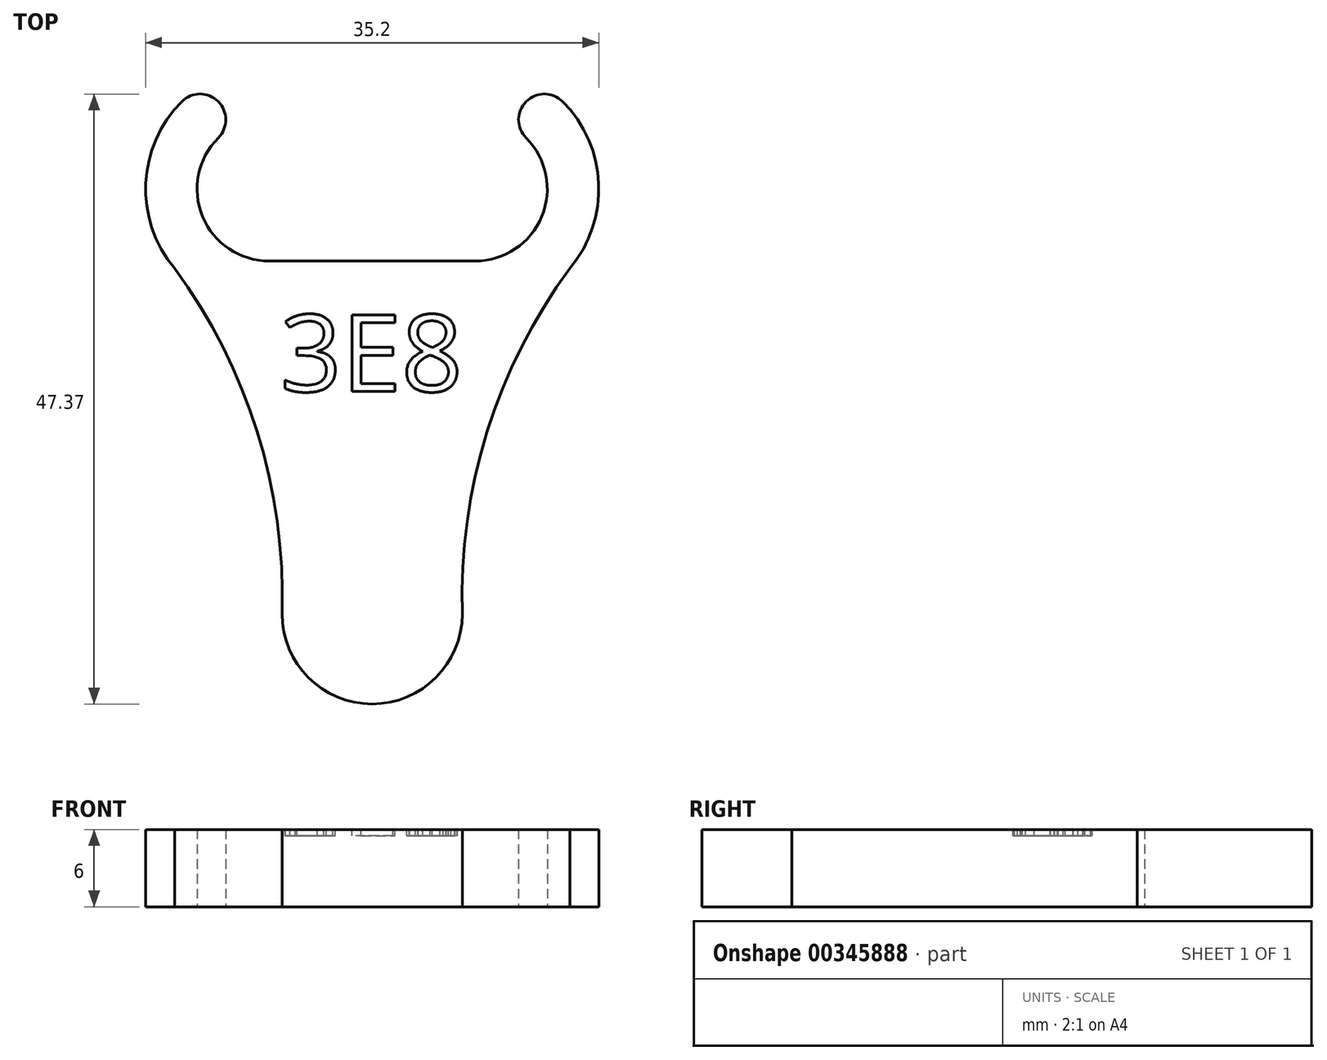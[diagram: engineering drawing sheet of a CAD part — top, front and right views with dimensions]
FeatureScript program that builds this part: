
annotation { "Feature Type Name" : "Feature", "Feature Type Description" : "" }
export const myFeature = defineFeature(function(context is Context, id is Id, definition is map)
    precondition{}
    {
        {
            assignVariable(context, id + "F0", {"name" : "toolthick", "anyValue" : 6});
        }
        {
            var Q0;
            Q0=qCreatedBy(makeId("Top.planeOp"),FACE);
            var sketch = newSketch(context, id + "F1", { "sketchPlane" : qUnion([Q0])});
            skLineSegment(sketch, "E0", {"start": v(-8, 0) * mm, "end": v(8, 0) * mm, "construction": true});
            skCircle(sketch, "E1", {"center": v(-8, 0) * mm, "radius": 5 * mm, "construction": true});
            skCircle(sketch, "E2", {"center": v(8, 0) * mm, "radius": 5 * mm, "construction": true});
            skArc(sketch, "E3", {"start": v(-13.6, 0) * mm, "mid": v(-11.96, -3.96) * mm, "end": v(-8, -5.6) * mm});
            skLineSegment(sketch, "E4", {"start": v(-8, 0) * mm, "end": v(-11.96, 3.96) * mm, "construction": true});
            skArc(sketch, "E5", {"start": v(-11.96, 3.96) * mm, "mid": v(-13.17, 2.14) * mm, "end": v(-13.6, 0) * mm});
            skArc(sketch, "E6", {"start": v(-11.96, 3.96) * mm, "mid": v(-11.96, 6.79) * mm, "end": v(-14.79, 6.79) * mm});
            skLineSegment(sketch, "E7", {"start": v(-11.96, 3.96) * mm, "end": v(-14.79, 6.79) * mm, "construction": true});
            skArc(sketch, "E8", {"start": v(-7, -33) * mm, "mid": v(-4.95, -37.95) * mm, "end": v(0, -40) * mm});
            skLineSegment(sketch, "E9", {"start": v(0, -40) * mm, "end": v(0, 0) * mm, "construction": true});
            skLineSegment(sketch, "E10", {"start": v(-8, -5.6) * mm, "end": v(0, -5.6) * mm});
            skLineSegment(sketch, "E11.MirrorCS", {"start": v(8, -5.6) * mm, "end": v(0, -5.6) * mm});
            skArc(sketch, "E12.MirrorCS", {"start": v(13.6, 0) * mm, "mid": v(11.96, -3.96) * mm, "end": v(8, -5.6) * mm});
            skArc(sketch, "E13.MirrorCS", {"start": v(11.96, 3.96) * mm, "mid": v(13.17, 2.14) * mm, "end": v(13.6, 0) * mm});
            skArc(sketch, "E14.MirrorCS", {"start": v(11.96, 3.96) * mm, "mid": v(11.96, 6.79) * mm, "end": v(14.79, 6.79) * mm});
            skArc(sketch, "E15.MirrorCS", {"start": v(7, -33) * mm, "mid": v(4.95, -37.95) * mm, "end": v(0, -40) * mm});
            skArc(sketch, "E16", {"start": v(-14.79, 6.79) * mm, "mid": v(-17.6, 0.42) * mm, "end": v(-15.35, -6.17) * mm});
            skArc(sketch, "E17.MirrorCS", {"start": v(14.79, 6.79) * mm, "mid": v(17.6, 0.42) * mm, "end": v(15.35, -6.17) * mm});
            skLineSegment(sketch, "E18", {"start": v(0, -33) * mm, "end": v(-7, -33) * mm, "construction": true});
            skLineSegment(sketch, "E19", {"start": v(-15.35, -6.17) * mm, "end": v(-8, 0) * mm, "construction": true});
            skArc(sketch, "E20", {"start": v(-7, -33) * mm, "mid": v(-8.92, -18.88) * mm, "end": v(-15.35, -6.17) * mm});
            skArc(sketch, "E21.MirrorCS", {"start": v(7, -33) * mm, "mid": v(8.92, -18.88) * mm, "end": v(15.35, -6.17) * mm});
            skSolve(sketch);
        }
        {
            var Q0;
            Q0 = qSketchRegion(id + "F1", true);
            extrude(context, id + "F2", {"entities" : qUnion([Q0]), "depth" : (getVariable(context, 'toolthick')) * mm});
        }
        {
            var Q0;
            Q0=makeQuery(id+"F2.opExtrude","CAP_FACE",FACE,{"disambiguationData":[OSD([sQuery(id+"F1.wireOp",EDGE,"E3"),sQuery(id+"F1.wireOp",EDGE,"E5"),sQuery(id+"F1.wireOp",EDGE,"E6"),sQuery(id+"F1.wireOp",EDGE,"9Umrm1ux-iD7h-QqVv-hRxH-csQvj10KXffC"),sQuery(id+"F1.wireOp",EDGE,"zTnV5ndj-D2DR-DuUr-h3Lb-husJmRXK0QGS"),sQuery(id+"F1.wireOp",EDGE,"E8"),sQuery(id+"F1.wireOp",EDGE,"E10"),sQuery(id+"F1.wireOp",EDGE,"E11.MirrorCS"),sQuery(id+"F1.wireOp",EDGE,"E12.MirrorCS"),sQuery(id+"F1.wireOp",EDGE,"E13.MirrorCS"),sQuery(id+"F1.wireOp",EDGE,"E14.MirrorCS"),sQuery(id+"F1.wireOp",EDGE,"958da9e3-6b30-4cd2-b741-3855218329e70.MirrorCS"),sQuery(id+"F1.wireOp",EDGE,"6e218b40-3901-4ca9-9324-4a29e95122480.MirrorCS"),sQuery(id+"F1.wireOp",EDGE,"E15.MirrorCS")])],"isStart":false});
            var sketch = newSketch(context, id + "F3", { "sketchPlane" : qUnion([Q0])});
            skText(sketch, "E22", { "text": "3E8", "fontName": "OpenSans-Regular.ttf"});
            skLineSegment(sketch, "E23", {"start": v(0, -5.6) * mm, "end": v(0, -9.73) * mm, "construction": true});
            const initialGuessF3  = {"E22": [-0.00714, -0.01573, 1, 0, 0.006]};
            skSetInitialGuess(sketch, initialGuessF3);
            skSolve(sketch);
        }
        {
            var Q0;
            Q0 = qSketchRegion(id + "F3", true);
            extrude(context, id + "F4", {"entities" : qUnion([Q0]), "operationType" : NewBodyOperationType.REMOVE, "oppositeDirection" : true, "depth" : .5 * mm});
        }
    });
